# Revit family: x1800 series-rev
name_source: partatom
category: Plumbing Fixtures
revit_build: Autodesk Revit 2018 (Build: 20170223_1515(x64)
units: mm (PartAtom-declared; Revit-internal decimal feet)

## family parameters
Always vertical = No
Cut with Voids When Loaded = No
OmniClass Number = 23.70.50.21.24.11
OmniClass Title = Roof Waste Water Drains
Part Type = Normal
Room Calculation Point = No
Round Connector Dimension = Use Diameter
Shared = Yes
Work Plane-Based = Yes

## types (15) — shared parameters
CW Connection = No
Deck Plate Material = Metal-Jay R Smith - Stainless Steel
Default Elevation = 0"
Description = Roof and Overflow Drain with Decktop Mounting Plate
Diameter = 15 1/4"
Dome Material = Plastic-Jay R Smith-Polyethylene
Drain Material = Cast Iron-Jay R Smith-Duco Coated
HW Connection = No
Installation Type = Roof
Length = 48"
Manufacturer = Jay R. Smith
Model = 1800
Product Documentation Link = https://www.jrsmith.com
Product Page URL = https://www.jrsmith.com
Standpipe Material = Polymer - Jay R Smith - PVC
URL = http://www.jrsmith.com
Vent Connection = No
Waste Connection = Yes
Width = 24"

## per-type parameters (varying)
| type | Connection Radius | Connection Size | Connection Type | Drain Height | Height | Stand Pipe Radius |
| 1800C02 | 1" | 2" | Caulk Outlet | 5" | 10 1/4" | 2" |
| 1800C03 | 1 1/2" | 3" | Caulk Outlet | 5" | 10 1/4" | 2" |
| 1800C04 | 2" | 4" | Caulk Outlet | 5" | 10 1/4" | 2" |
| 1800C05 | 2 1/2" | 5" | Caulk Outlet | 5" | 10 1/4" | 3" |
| 1800C06 | 3" | 6" | Caulk Outlet | 5" | 10 1/4" | 3" |
| 1800Y02 | 1" | 2" | No-HUB Outlet | 5" | 10 1/4" | 2" |
| 1800Y03 | 1 1/2" | 3" | No-HUB Outlet | 5" | 10 1/4" | 2" |
| 1800Y04 | 2" | 4" | No-HUB Outlet | 5" | 10 1/4" | 2" |
| 1800Y05 | 2 1/2" | 5" | No-HUB Outlet | 5" | 10 1/4" | 3" |
| 1800Y06 | 3" | 6" | No-HUB Outlet | 5" | 10 1/4" | 3" |
| 1800T06 | 3" | 6" | Threaded | 3 3/4" | 9" | 3" |
| 1800T05 | 2 1/2" | 5" | Threaded | 3 3/4" | 9" | 3" |
| 1800T04 | 2" | 4" | Threaded | 3 3/4" | 9" | 2" |
| 1800T03 | 1 1/2" | 3" | Threaded | 3 3/4" | 9" | 2" |
| 1800T02 | 1" | 2" | Threaded | 3 3/4" | 9" | 2" |

## geometry (parser evidence)
native form markers: Sweep x2
no freeform markers — native parametric forms only
